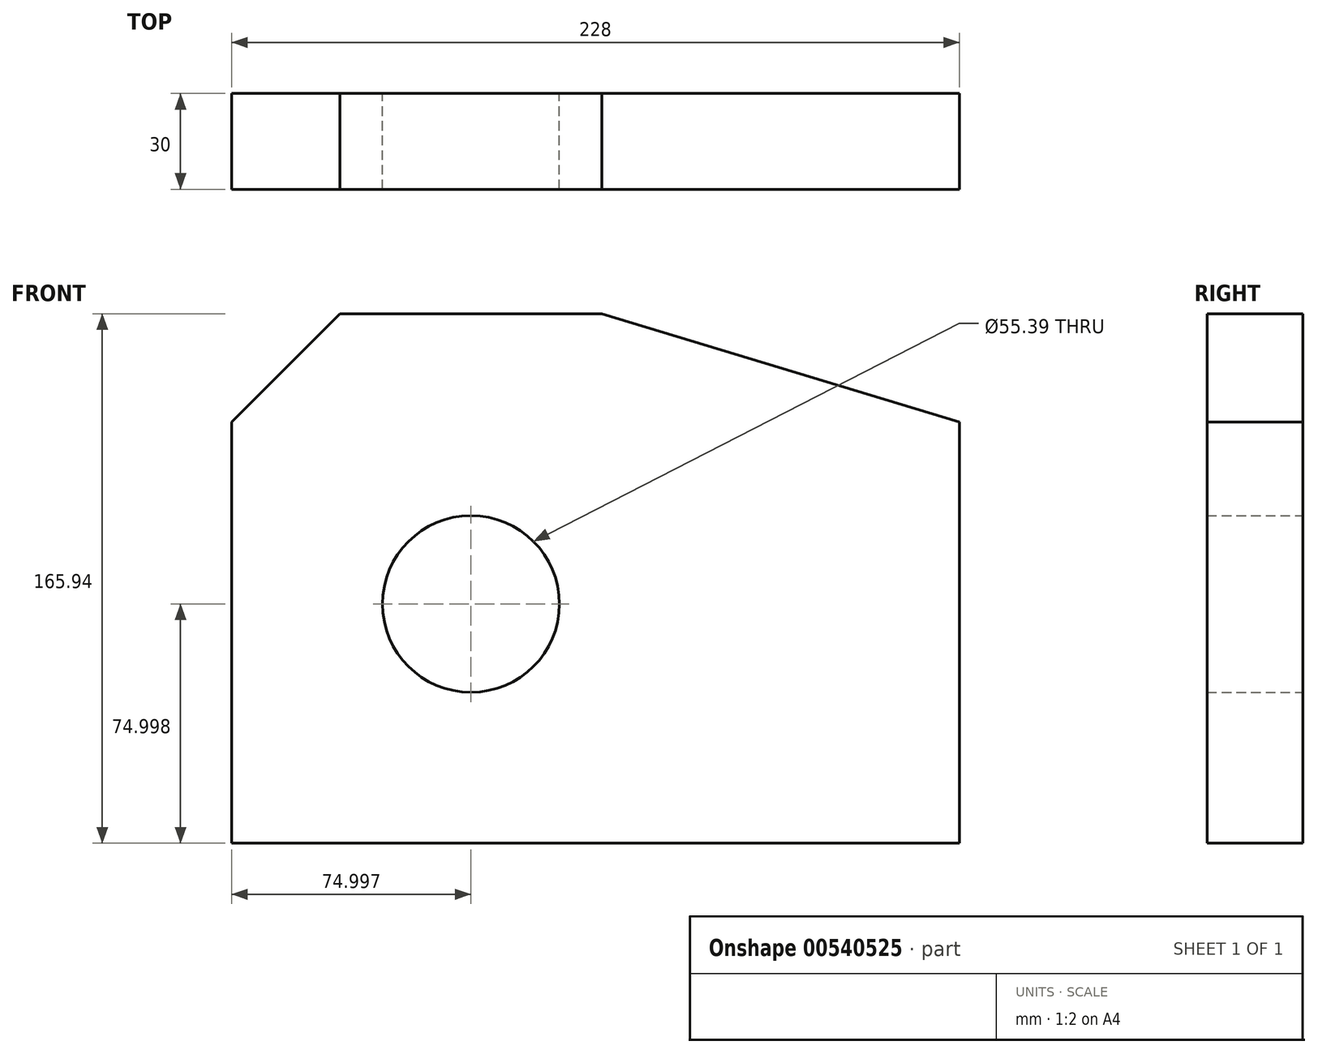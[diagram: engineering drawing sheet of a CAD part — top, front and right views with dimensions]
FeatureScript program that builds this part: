
annotation { "Feature Type Name" : "Feature", "Feature Type Description" : "" }
export const myFeature = defineFeature(function(context is Context, id is Id, definition is map)
    precondition{}
    {
        {
            var Q0;
            Q0=qCreatedBy(makeId("Front.planeOp"),FACE);
            var sketch = newSketch(context, id + "F0", { "sketchPlane" : qUnion([Q0])});
            skLineSegment(sketch, "E0", {"start": v(-140.81, 27.62) * mm, "end": v(-140.81, -104.38) * mm});
            skLineSegment(sketch, "E1", {"start": v(-140.81, -104.38) * mm, "end": v(87.19, -104.38) * mm});
            skLineSegment(sketch, "E2", {"start": v(87.19, -104.38) * mm, "end": v(87.19, 27.62) * mm});
            skLineSegment(sketch, "E3", {"start": v(87.19, 27.62) * mm, "end": v(-24.78, 61.56) * mm});
            skLineSegment(sketch, "E4", {"start": v(-24.78, 61.56) * mm, "end": v(-106.87, 61.56) * mm});
            skLineSegment(sketch, "E5", {"start": v(-106.87, 61.56) * mm, "end": v(-140.81, 27.62) * mm});
            skCircle(sketch, "E6", {"center": v(-65.81, -29.38) * mm, "radius": 27.7 * mm});
            skSolve(sketch);
        }
        {
            var Q0;
            Q0 = qSketchRegion(id + "F0", true);
            extrude(context, id + "F1", {"entities" : qUnion([Q0]), "depth" : 30 * mm, "offsetDistance" : 25 * mm});
        }
    });
